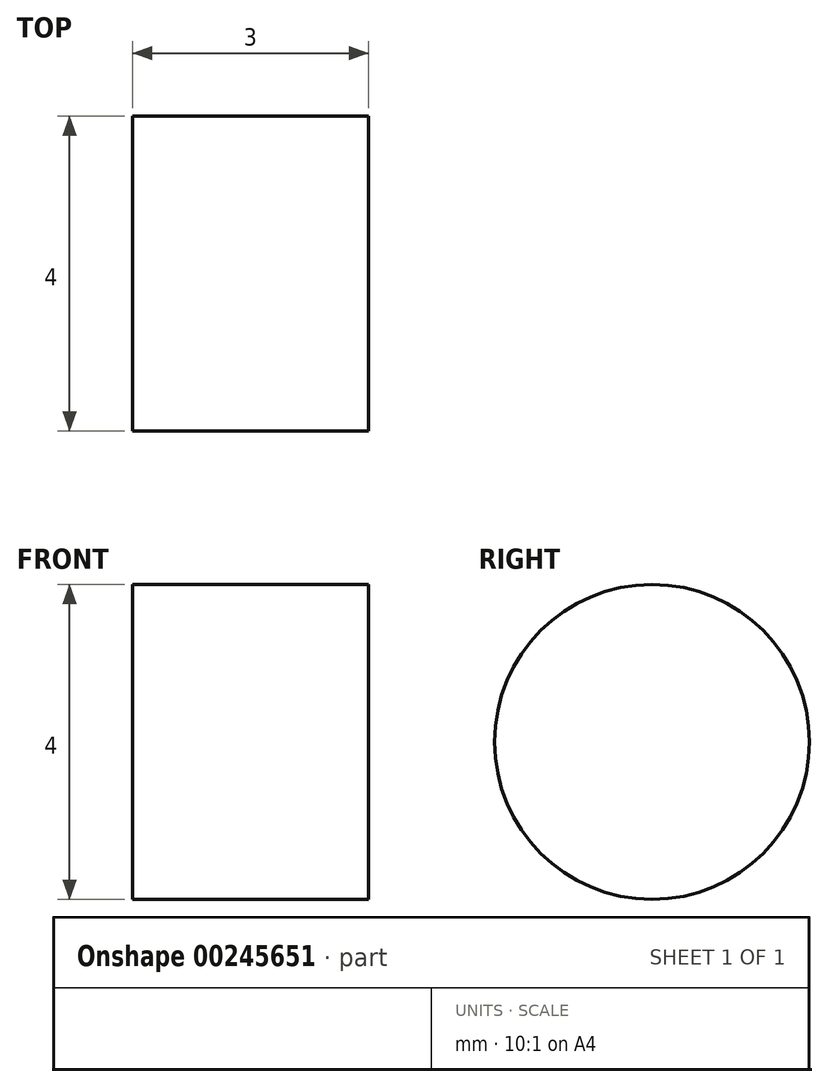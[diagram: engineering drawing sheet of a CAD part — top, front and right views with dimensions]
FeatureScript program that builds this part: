
annotation { "Feature Type Name" : "Feature", "Feature Type Description" : "" }
export const myFeature = defineFeature(function(context is Context, id is Id, definition is map)
    precondition{}
    {
        {
            var Q0;
            Q0=qCreatedBy(makeId("Right.planeOp"),FACE);
            var sketch = newSketch(context, id + "F0", { "sketchPlane" : qUnion([Q0])});
            skCircle(sketch, "E0", {"center": v(0, 0) * mm, "radius": 2 * mm});
            skSolve(sketch);
        }
        {
            var Q0;
            Q0=makeQuery(id+"F0.imprint","IMPRINT",FACE,{"disambiguationData":[TD([[makeQuery(id+"F0.imprint","IMPRINT",EDGE,{"derivedFrom":sQuery(id+"F0.wireOp",EDGE,"E0")}),1.0]])]});
            extrude(context, id + "F1", {"entities" : qUnion([Q0]), "depth" : 3 * mm, "offsetDistance" : 25 * mm});
        }
    });
